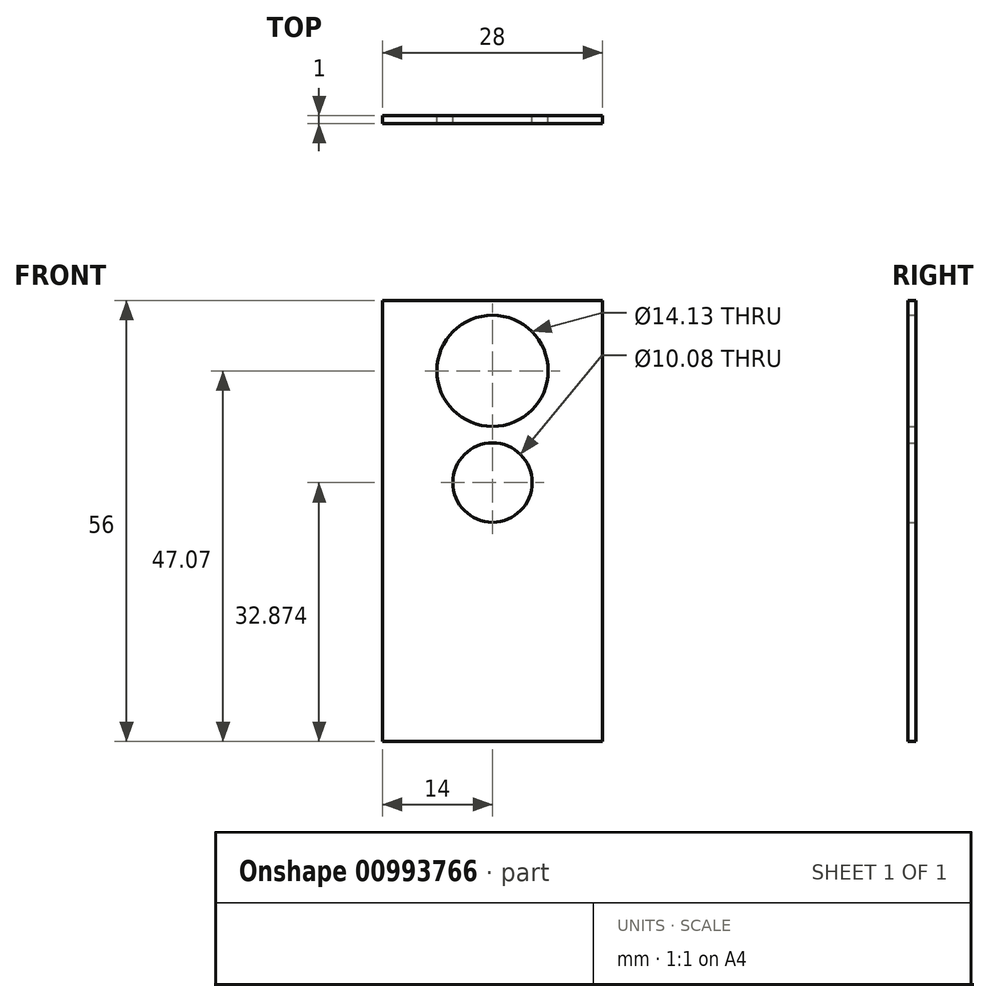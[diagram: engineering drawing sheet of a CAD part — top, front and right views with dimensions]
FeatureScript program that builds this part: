
annotation { "Feature Type Name" : "Feature", "Feature Type Description" : "" }
export const myFeature = defineFeature(function(context is Context, id is Id, definition is map)
    precondition{}
    {
        {
            var Q0;
            Q0=qCreatedBy(makeId("Front.planeOp"),FACE);
            var sketch = newSketch(context, id + "F0", { "sketchPlane" : qUnion([Q0])});
            skLineSegment(sketch, "E0.bottom", {"start": v(14, 28) * mm, "end": v(-14, 28) * mm});
            skLineSegment(sketch, "E0.top", {"start": v(14, -28) * mm, "end": v(-14, -28) * mm});
            skLineSegment(sketch, "E0.left", {"start": v(14, 28) * mm, "end": v(14, -28) * mm});
            skLineSegment(sketch, "E0.right", {"start": v(-14, 28) * mm, "end": v(-14, -28) * mm});
            skPoint(sketch, "E0.middle", {"position": v(0, 0) * mm});
            skCircle(sketch, "E1", {"center": v(0, 19.07) * mm, "radius": 7.07 * mm});
            skPoint(sketch, "E1.centerSnap0", {"position": v(0, 28) * mm});
            skCircle(sketch, "E2", {"center": v(0, 4.87) * mm, "radius": 5.04 * mm});
            skSolve(sketch);
        }
        {
            var Q0;
            Q0 = qSketchRegion(id + "F0", true);
            extrude(context, id + "F1", {"entities" : qUnion([Q0]), "depth" : 1 * mm, "offsetDistance" : 25 * mm});
        }
    });
